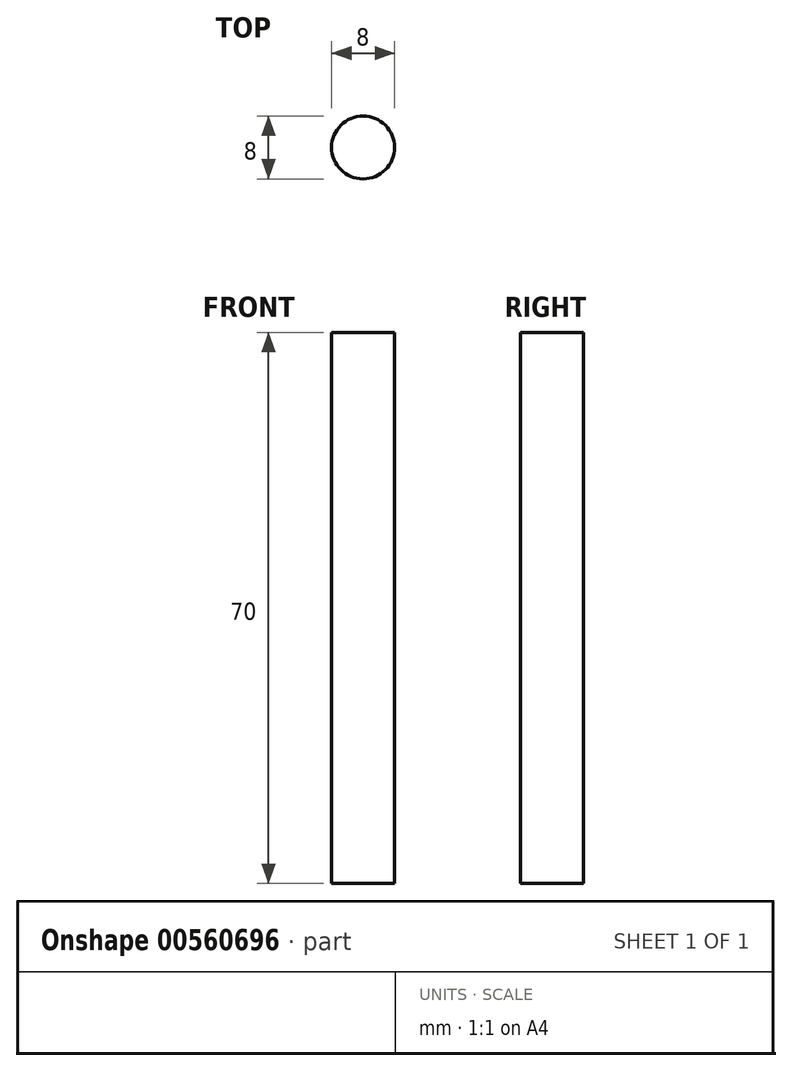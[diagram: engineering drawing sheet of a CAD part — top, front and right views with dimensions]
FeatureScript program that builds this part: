
annotation { "Feature Type Name" : "Feature", "Feature Type Description" : "" }
export const myFeature = defineFeature(function(context is Context, id is Id, definition is map)
    precondition{}
    {
        {
            var Q0;
            Q0=qCreatedBy(makeId("Top.planeOp"),FACE);
            var sketch = newSketch(context, id + "F0", { "sketchPlane" : qUnion([Q0])});
            skCircle(sketch, "E0", {"center": v(0, 0) * mm, "radius": 4 * mm});
            skSolve(sketch);
        }
        {
            var Q0;
            Q0=qCreatedBy(makeId("Front.planeOp"),FACE);
            var sketch = newSketch(context, id + "F1", { "sketchPlane" : qUnion([Q0])});
            skLineSegment(sketch, "E1", {"start": v(0, 0) * mm, "end": v(0, 70) * mm});
            skSolve(sketch);
        }
        {
            var Q0;
            Q0=makeQuery(id+"F0.imprint","IMPRINT",FACE,{"disambiguationData":[TD([[makeQuery(id+"F0.imprint","IMPRINT",EDGE,{"derivedFrom":sQuery(id+"F0.wireOp",EDGE,"E0")}),1.0]])]});
            var Q1;
            Q1=sQuery(id+"F1.wireOp",EDGE,"E1");
            sweep(context, id + "F2", {"profiles" : qUnion([Q0]), "path" : qUnion([Q1])});
        }
    });
